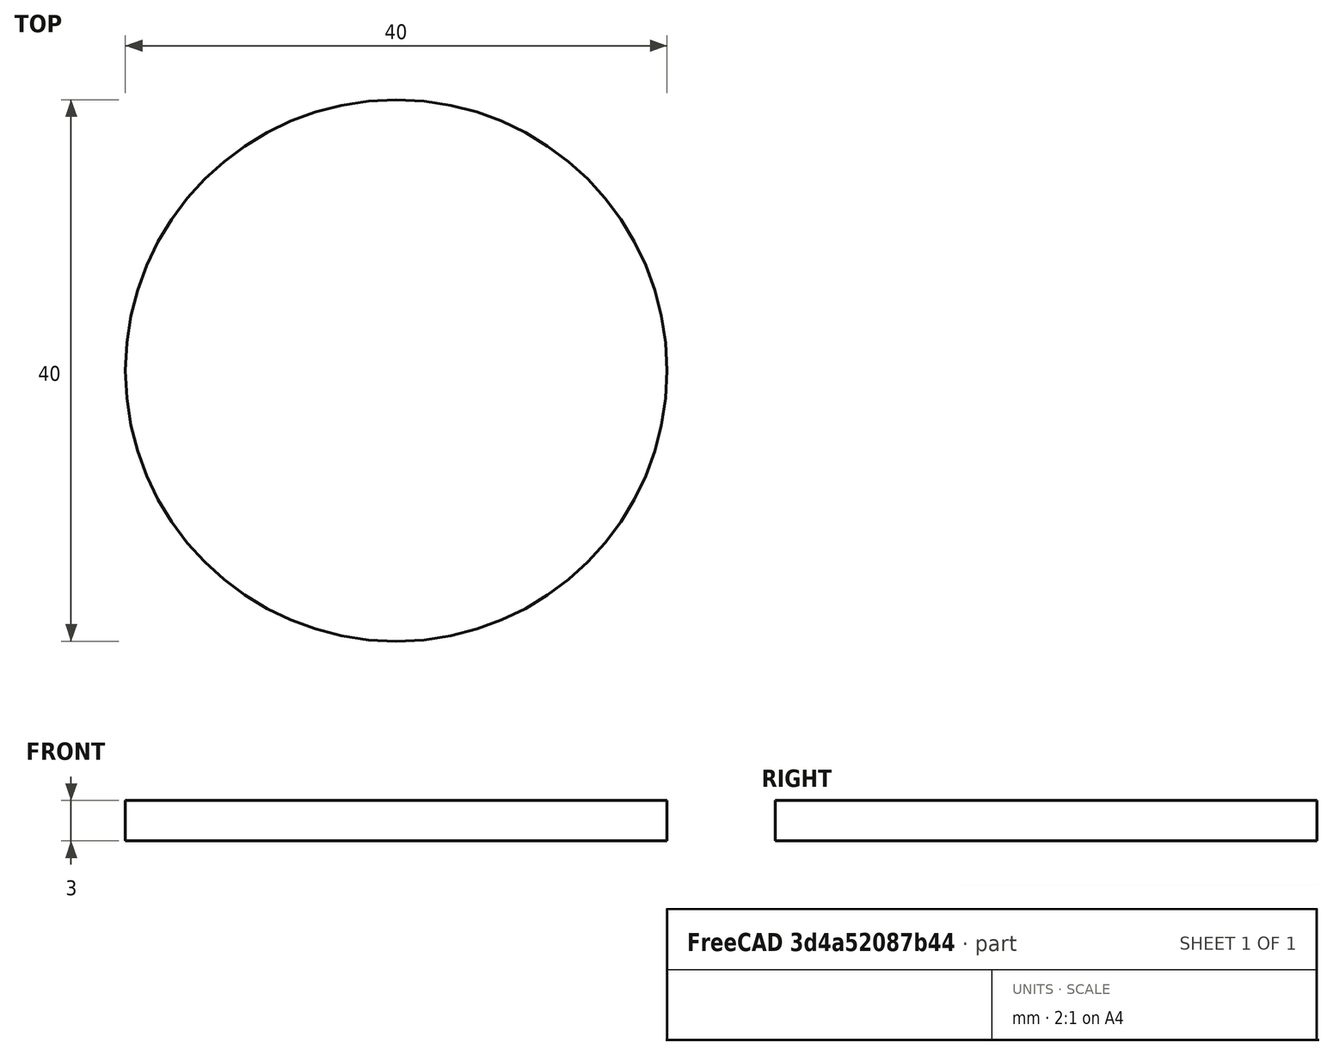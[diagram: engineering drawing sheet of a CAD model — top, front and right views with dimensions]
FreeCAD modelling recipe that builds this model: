
FCSTD DOCUMENT  (FreeCAD 0.20R29177 +233 (Git))
Label: L4-EJ1
License: Creative Commons Attribution-ShareAlike
LicenseURL: http://creativecommons.org/licenses/by-sa/4.0/
objects: Part::Extrusion×2, Sketcher::SketchObject×1
note: 3 computed .brp shape members not serialized (recipe doc carries the construction recipe); baked Part::Feature solids carry a one-line shape summary decoded from their .brp

FEATURE [Sketcher::SketchObject] Sketch
  FullyConstrained = true
  sketch-geometry (1):
    g0: Circle CenterX=0 CenterY=0 CenterZ=0 NormalX=0 NormalY=0 NormalZ=1 AngleXU=0 Radius=20
  constraints (2):
    c: Coincident(g0,g-1)
    c: Diameter(g0) = 40
FEATURE [Part::Extrusion] Extrude
  Base = -> Sketch
  Dir = (0,0,1)
  DirMode = 2
  FaceMakerClass = Part::FaceMakerBullseye
  LengthFwd = 3
  LengthRev = 0
  Solid = true
  Symmetric = false
FEATURE [Part::Extrusion] Extrude001
  Base = -> Sketch
  Dir = (0,0,1)
  DirMode = 2
  FaceMakerClass = Part::FaceMakerBullseye
  LengthFwd = 3
  LengthRev = 0
  Solid = true
  Symmetric = false
